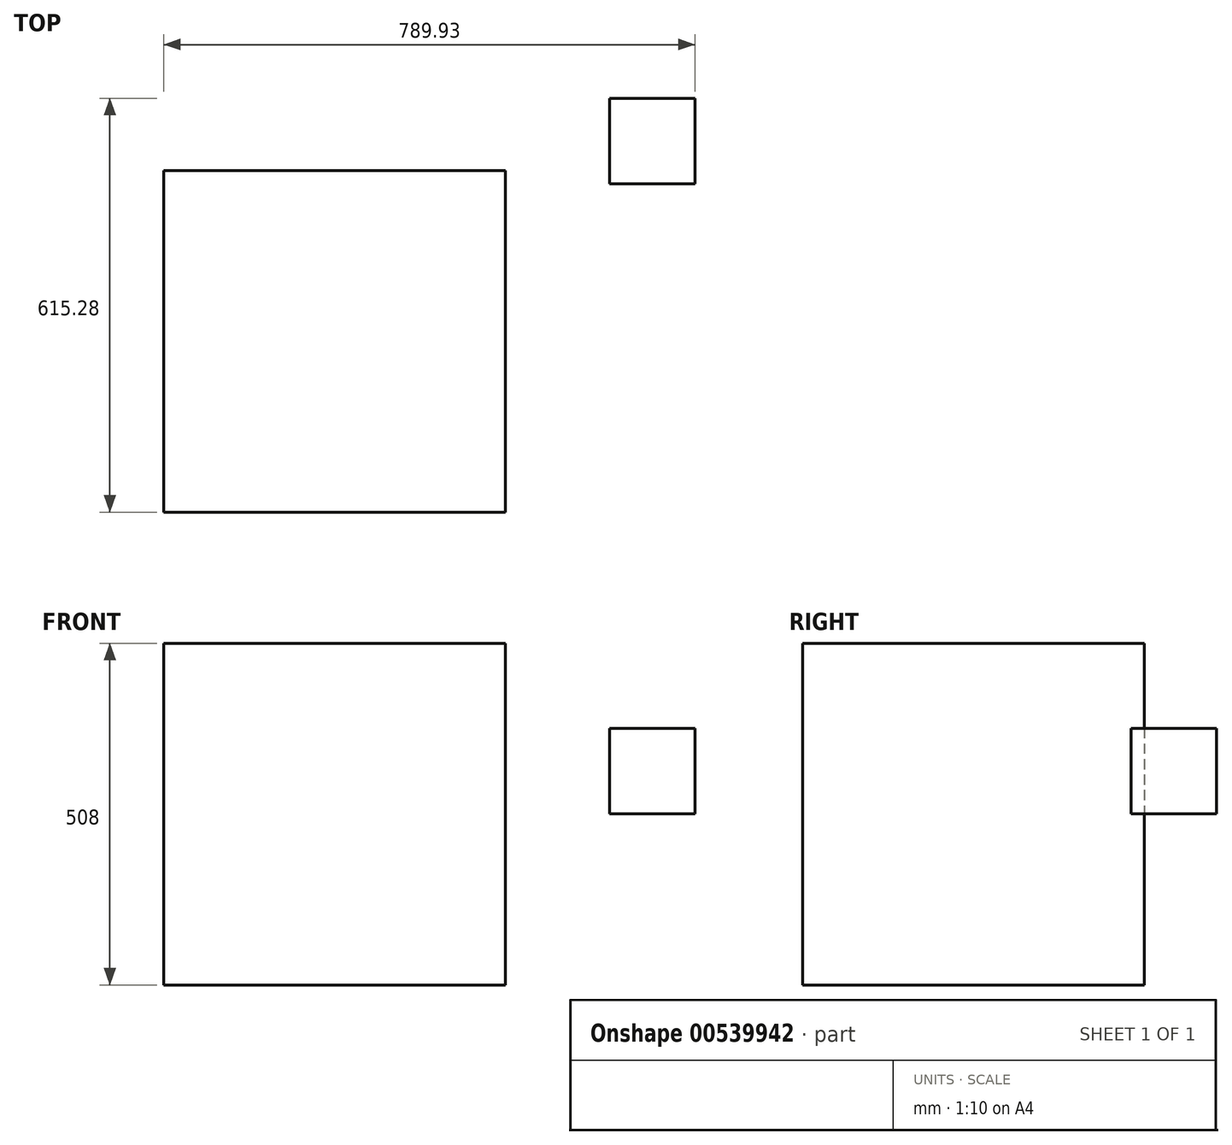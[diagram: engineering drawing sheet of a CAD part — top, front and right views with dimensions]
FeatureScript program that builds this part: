
annotation { "Feature Type Name" : "Feature", "Feature Type Description" : "" }
export const myFeature = defineFeature(function(context is Context, id is Id, definition is map)
    precondition{}
    {
        {
            var Q0;
            Q0=qCreatedBy(makeId("Front.planeOp"),FACE);
            var sketch = newSketch(context, id + "F0", { "sketchPlane" : qUnion([Q0])});
            skLineSegment(sketch, "E0", {"start": v(-381.54, 253.34) * mm, "end": v(126.46, 253.34) * mm});
            skLineSegment(sketch, "E1", {"start": v(126.46, 253.34) * mm, "end": v(126.46, -254.66) * mm});
            skLineSegment(sketch, "E2", {"start": v(126.46, -254.66) * mm, "end": v(-381.54, -254.66) * mm});
            skLineSegment(sketch, "E3", {"start": v(-381.54, -254.66) * mm, "end": v(-381.54, 253.34) * mm});
            skSolve(sketch);
        }
        {
            var Q0;
            Q0=makeQuery(id+"F0.imprint","IMPRINT",FACE,{"disambiguationData":[TD([[makeQuery(id+"F0.imprint","IMPRINT",EDGE,{"derivedFrom":sQuery(id+"F0.wireOp",EDGE,"E0")}),-1.0]])]});
            extrude(context, id + "F1", {"entities" : qUnion([Q0]), "depth" : 508 * mm, "offsetDistance" : 25.4 * mm});
        }
        {
            var Q0;
            Q0=qCreatedBy(makeId("Top.planeOp"),FACE);
            var sketch = newSketch(context, id + "F2", { "sketchPlane" : qUnion([Q0])});
            skLineSegment(sketch, "E4", {"start": v(408.39, 107.28) * mm, "end": v(281.39, 107.28) * mm});
            skLineSegment(sketch, "E5", {"start": v(281.39, 107.28) * mm, "end": v(281.39, -19.72) * mm});
            skLineSegment(sketch, "E6", {"start": v(281.39, -19.72) * mm, "end": v(408.39, -19.72) * mm});
            skLineSegment(sketch, "E7", {"start": v(408.39, -19.72) * mm, "end": v(408.39, 107.28) * mm});
            skSolve(sketch);
        }
        {
            var Q0;
            Q0 = qSketchRegion(id + "F2", true);
            extrude(context, id + "F3", {"entities" : qUnion([Q0]), "depth" : 127 * mm, "offsetDistance" : 25.4 * mm});
        }
    });
